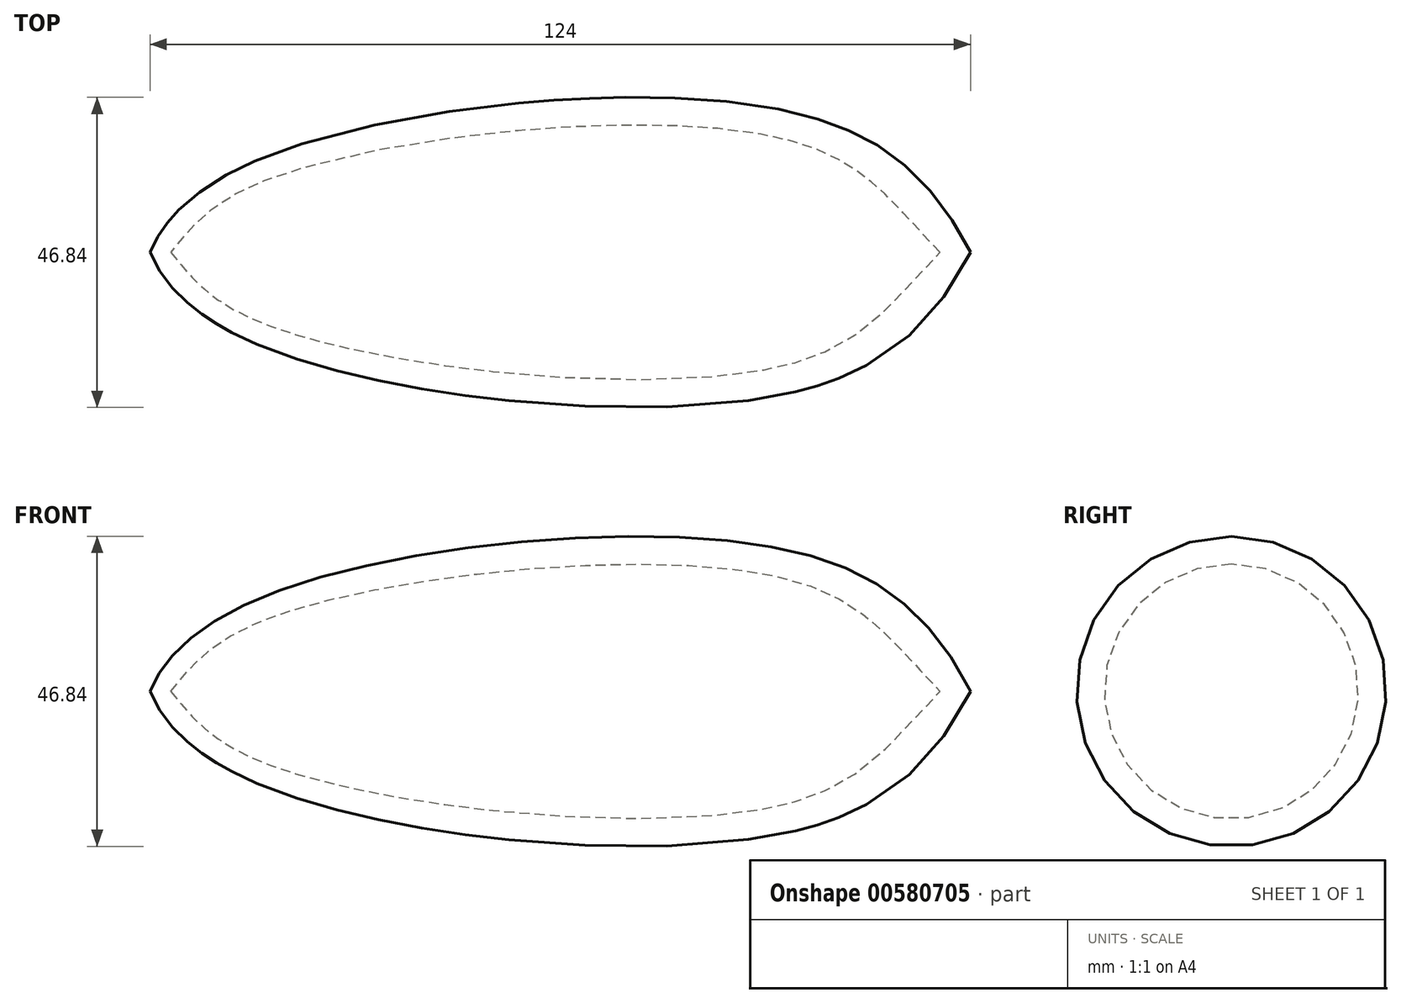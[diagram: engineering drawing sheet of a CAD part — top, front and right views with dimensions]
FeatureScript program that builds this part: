
annotation { "Feature Type Name" : "Feature", "Feature Type Description" : "" }
export const myFeature = defineFeature(function(context is Context, id is Id, definition is map)
    precondition{}
    {
        {
            var Q0;
            Q0=qCreatedBy(makeId("Front.planeOp"),FACE);
            var sketch = newSketch(context, id + "F0", { "sketchPlane" : qUnion([Q0])});
            skFitSpline(sketch, "E0", {"points": [v(-68.2, 0) * mm, v(-51.75, 14.05) * mm, v(23.46, 22.21) * mm, v(55.8, 0) * mm], "startDerivative": vector(24.27, 61.77) * mm, "endDerivative": vector(65.41, -128.07) * mm});
            skLineSegment(sketch, "E1", {"start": v(-68.2, 0) * mm, "end": v(-65.11, 0) * mm});
            skLineSegment(sketch, "E2", {"start": v(55.8, 0) * mm, "end": v(51.2, 0) * mm});
            skFitSpline(sketch, "E3", {"points": [v(-65.11, 0) * mm, v(-51.14, 10.74) * mm, v(28.46, 16.9) * mm, v(51.2, 0) * mm], "startDerivative": vector(41.13, 49.29) * mm, "endDerivative": vector(72.6, -73.15) * mm});
            skLineSegment(sketch, "E4", {"start": v(-68.2, 0) * mm, "end": v(55.8, 0) * mm});
            skSolve(sketch);
        }
        {
            var Q0;
            {var subQ0=sQuery(id+"F0.wireOp",EDGE,"E0");Q0=makeQuery(id+"F0.imprint","IMPRINT",FACE,{"disambiguationData":[TD([[makeQuery(id+"F0.imprint","IMPRINT",EDGE,{"derivedFrom":subQ0}),-1.0]])]});}
            var Q1;
            Q1=sQuery(id+"F0.wireOp",EDGE,"E4");
            revolve(context, id + "F1", {"entities" : qUnion([Q0]), "axis" : qUnion([Q1]), "revolveType" : RevolveType.FULL});
        }
    });
